# Revit family: Kamstrup_Multical_602+Ultraflow 54 резьбовые
name_source: partatom
category: Арматура трубопроводов
revit_build: Autodesk Revit 2016 (Build: 20150714_1515(x64)
units: mm (PartAtom-declared; Revit-internal decimal feet)

## family parameters
Всегда вертикально = Да
На основе рабочей плоскости = Нет
Общий = Нет
При загрузке вырезать с полостями = Нет
Размер круглого соединителя = Использовать диаметр
Тип детали = Встроенный датчик

## types (10) — shared parameters
150 = 150 мм
H1 = 55 мм
ID01 = 0 Без модуля верха
ID02 = 2 Расчет дельты энергий + почасовой архив
ID03 = 3 PQ или дельта t-ограничитель + почасовой архив
ID04 = 5 Выход данных + почасовой архив
ID05 = 7 M-BUS
ID06 = 9 Расчет дельты объемов +почасовой архив
ID07 = A 2 имп.выхода CE и CV + почасовой архив +расписание
ID08 = B ЧРВ + 2 имп.выхода CE и CV + программируемый архив
ID09 = C 2 имп.выхода CE и CV
ID10 = 00 Без модуля низа
ID11 = 10 Данные + импульсные входы
ID12 = 20 M-Bus + импульсные входы
ID13 = 21 Радио Роутер + импульсные входы
ID14 = 22 Программируемый архив + ЧРВ + входы 4…20 мA + имп.Входы
ID15 = 23 0/4…20 мA выходы : 23 4…20 мA выходы
ID16 = 24 LonWorks + импульсные входы
ID17 = 25 Радио + имп.входы (встроенная антенна) 434 или 444 МГц
ID18 = 26 Радио + имп.входы (для внешней антенны) 434 или 444 МГц
ID19 = 27 M-Bus с альтернативными регистрами + имп.входы
ID20 = 28 M-Bus с пакетом данных M-size + имп.входы
ID21 = 29 M-Bus с MC-III совместимым пакетом данных + имп.Входы
ID22 = 30 Беспроводной M-Bus Mode C1 + 2 импульсных входа (VA, VB) (инд.ключ шифрования)
ID23 = 31 Беспроводной M-Bus, Режим T1 OMS 15 мин. (инд.ключ)
ID24 = 35 Беспроводной M-Bus Mode C1 с альт. регистр. + 2 имп. вх.(VA, VB)
ID25 = 36 Беспроводной M-Bus, Режим T1 OMS 16 сек. (инд.ключ)
ID26 = 38 Беспроводной M-Bus, C1, для стационарных сетей, (инд.ключ)
ID27 = 39 Беспроводной M-Bus, C1, для стационарных сетей, (инд.ключ), PDO Data
ID28 = 60 ZigBee 2.4 ГГц встроенная антенна + 2 имп.входа (VA, VB)
ID29 = 62 Metasys N2 (RS485) + 2 импульсных входа (VA, VB)
ID30 = 64 SIOX модуль (Автоматическое определение скорости)
ID31 = 66 BACnetMS/TP + импульсный входы : 66  TP + импульсный входы
ID32 = 67 Modbus RTU + импульсный входы
ID33 = 2 Батарея, D-элемент
ID36 = 00 Без датчика температуры
ID37 = 0A Пара датчиков для гильз кабель 1,5 м
ID38 = 0B Пара датчиков для гильз кабель 3,0 м
ID39 = 0C Пара датчиков для гильз кабель 5 м
ID40 = 0D Пара датчиков для гильз кабель 10 м
ID41 = 0F Пара коротких датчиков прямого погружения кабель 1,5 м
ID42 = 0G Пара коротких датчиков прямого погружения кабель 3,0 м
ID43 = 0L Комплект из 3 датчиков для гильз кабель 1,5 м
ID44 = Q3 Комплект из 3 коротких датчиков прям.погружения кабель 1,5 м
ID45 = 7 Для одного ULTRAFLOW
ID46 = 8 Для двух (одинаковых) ULTRAFLOW
ID47 = 4 Теплосчетчик, национальная сертификация
ID48 = 5 Счетчик энергии охлаждения (TS27.02+DK268)
ID49 = 9 Счетчик энергии
URL = https://www.kamstrup.com
Адрес = 141008, Московская обл., г. Мытищи, ул. Колпакова, 26
Изготовитель = ЗАО «Камструп»
Таблица выбора = multical 602
Телефон = +7 495 545 00 01
Тип счетчика = 4 Теплосчетчик, национальная сертификация

## per-type parameters (varying)
| type | A | B1 | B2 | DN | DN_стенка | G | H2 | ID34 | ID35 | L | M | RN_стенка | Тип | видимость_H | видимость_неH |
| 65-5- CAHA | 8 мм | 37 мм | 32 мм | 15 мм | 17 мм | 20 мм | 86 мм | 7 230 В AC изолированный линейный | 8 24 В AC изолированный линейный | 110 мм | 55 мм | 9 мм | Ultraflow 65-5- CAHA | Да | Нет |
| 65-5- CAHD | 12 мм | 37 мм | 32 мм | 20 мм | 23 мм | 25 мм | 86 мм | 7 230 В AC изолированный линейный | 8 24 В AC изолированный линейный | 110 мм | 55 мм | 12 мм | Ultraflow 65-5- CAHD | Да | Нет |
| 65-5- CDHA | 12 мм | 37 мм | 32 мм | 15 мм | 17 мм | 20 мм | 86 мм | 7 230 В AC изолированный линейный | 8 24 В AC изолированный линейный | 130 мм | 65 мм | 9 мм | Ultraflow 65-5- CDHA | Да | Нет |
| 65-5- CDHC | 12 мм | 40 мм | 35 мм | 15 мм | 17 мм | 20 мм | 86 мм | 7 230 В AC изолированный линейный | 8 24 В AC изолированный линейный | 130 мм | 65 мм | 9 мм | Ultraflow 65-5- CDHC | Да | Нет |
| 65-5- CDHD | 8 мм | 37 мм | 32 мм | 20 мм | 23 мм | 25 мм | 86 мм | 2 Батарея, D-элемент | 2 Батарея, D-элемент | 165 мм | 83 мм | 12 мм | Ultraflow 65-5- CDHD | Да | Нет |
| 65-5- CDHF | 12 мм | 37 мм | 32 мм | 20 мм | 23 мм | 25 мм | 86 мм | 7 230 В AC изолированный линейный | 8 24 В AC изолированный линейный | 190 мм | 95 мм | 12 мм | Ultraflow 65-5- CDHF | Да | Нет |
| 65-5- CEHF | 12 мм | 40 мм | 35 мм | 20 мм | 23 мм | 25 мм | 86 мм | 7 230 В AC изолированный линейный | 8 24 В AC изолированный линейный | 190 мм | 95 мм | 12 мм | Ultraflow 65-5- CEHF | Да | Нет |
| 65-5- CGAG | 17 мм | 58 мм | 22 мм | 25 мм | 29 мм | 32 мм | 89 мм | 7 230 В AC изолированный линейный | 8 24 В AC изолированный линейный | 260 мм | 130 мм | 14 мм | Ultraflow 65-5- CGAG | Нет | Да |
| 65-5- CHAG | 17 мм | 58 мм | 22 мм | 25 мм | 29 мм | 32 мм | 89 мм | 7 230 В AC изолированный линейный | 8 24 В AC изолированный линейный | 260 мм | 130 мм | 14 мм | Ultraflow 65-5- CHAG | Нет | Да |
| 65-5- CJAJ | 21 мм | 65 мм | 31 мм | 40 мм | 46 мм | 50 мм | 86 мм | 7 230 В AC изолированный линейный | 8 24 В AC изолированный линейный | 300 мм | 150 мм | 23 мм | Ultraflow 65-5- CJAJ | Нет | Да |

## geometry (parser evidence)
native form markers: Blend x2
no freeform markers — native parametric forms only
